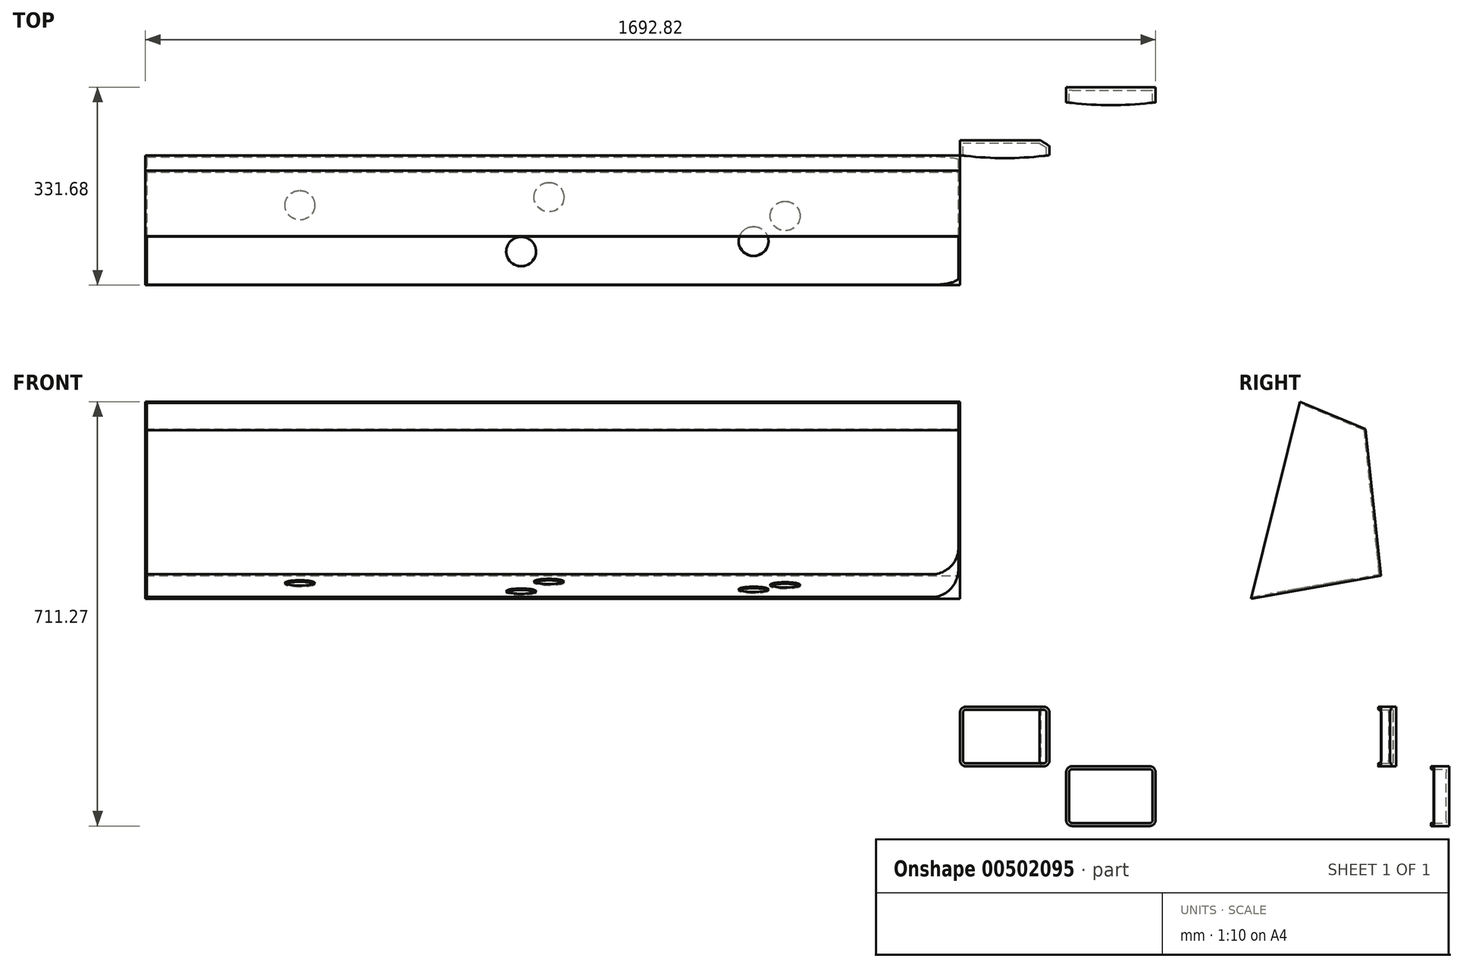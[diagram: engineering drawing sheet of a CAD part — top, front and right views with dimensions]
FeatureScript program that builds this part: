
annotation { "Feature Type Name" : "Feature", "Feature Type Description" : "" }
export const myFeature = defineFeature(function(context is Context, id is Id, definition is map)
    precondition{}
    {
        {
            var Q0;
            Q0=qCreatedBy(makeId("Front.planeOp"),FACE);
            var sketch = newSketch(context, id + "F0", { "sketchPlane" : qUnion([Q0])});
            skLineSegment(sketch, "E0.bottom", {"start": v(0, 0) * mm, "end": v(150, 0) * mm});
            skLineSegment(sketch, "E0.top", {"start": v(0, 100) * mm, "end": v(150, 100) * mm});
            skLineSegment(sketch, "E0.left", {"start": v(0, 0) * mm, "end": v(0, 100) * mm});
            skLineSegment(sketch, "E0.right", {"start": v(150, 0) * mm, "end": v(150, 100) * mm});
            skSolve(sketch);
        }
        {
            var Q0;
            Q0=makeQuery(id+"F0.imprint","IMPRINT",FACE,{"disambiguationData":[TD([[makeQuery(id+"F0.imprint","IMPRINT",EDGE,{"derivedFrom":sQuery(id+"F0.wireOp",EDGE,"E0.bottom")}),1.0]])]});
            extrude(context, id + "F1", {"entities" : qUnion([Q0]), "depth" : 30 * mm});
        }
        {
            var Q0;
            Q0=makeQuery(id+"F1.opExtrude","SWEPT_EDGE",EDGE,{"disambiguationData":[OSD([sQuery(id+"F0.wireOp",EDGE,"E0.top"),sQuery(id+"F0.wireOp",EDGE,"E0.left")])]});
            var Q1;
            Q1=makeQuery(id+"F1.opExtrude","SWEPT_EDGE",EDGE,{"disambiguationData":[OSD([sQuery(id+"F0.wireOp",EDGE,"E0.bottom"),sQuery(id+"F0.wireOp",EDGE,"E0.left")])]});
            var Q2;
            Q2=makeQuery(id+"F1.opExtrude","SWEPT_EDGE",EDGE,{"disambiguationData":[OSD([sQuery(id+"F0.wireOp",EDGE,"E0.bottom"),sQuery(id+"F0.wireOp",EDGE,"E0.right")])]});
            var Q3;
            Q3=makeQuery(id+"F1.opExtrude","SWEPT_EDGE",EDGE,{"disambiguationData":[OSD([sQuery(id+"F0.wireOp",EDGE,"E0.top"),sQuery(id+"F0.wireOp",EDGE,"E0.right")])]});
            fillet(context, id + "F2", {"entities" : qUnion([Q0, Q1, Q2, Q3]), "radius" : 10 * mm, "tangentPropagation" : true, "allowEdgeOverflow" : false});
        }
        {
            var Q0;
            Q0=makeQuery(id+"F1.opExtrude","CAP_FACE",FACE,{"disambiguationData":[OSD([sQuery(id+"F0.wireOp",EDGE,"E0.bottom"),sQuery(id+"F0.wireOp",EDGE,"E0.top"),sQuery(id+"F0.wireOp",EDGE,"E0.left"),sQuery(id+"F0.wireOp",EDGE,"E0.right")])],"isStart":false});
            shell(context, id + "F3", {"entities" : qUnion([Q0]), "thickness" : 5 * mm});
        }
        {
            var Q0;
            Q0=makeQuery(id+"F1.opExtrude","SWEPT_FACE",FACE,{"disambiguationData":[OSD([sQuery(id+"F0.wireOp",EDGE,"E0.bottom")])]});
            var sketch = newSketch(context, id + "F4", { "sketchPlane" : qUnion([Q0])});
            skLineSegment(sketch, "E1.0", {"start": v(10, 30) * mm, "end": v(140, 30) * mm});
            skLineSegment(sketch, "E2.0", {"start": v(0, 0) * mm, "end": v(0, 30) * mm});
            skLineSegment(sketch, "E3", {"start": v(75, 30) * mm, "end": v(75, -535) * mm});
            skCircle(sketch, "E4", {"center": v(75, -535) * mm, "radius": 565 * mm});
            skPoint(sketch, "E5", {"position": v(0, 25) * mm});
            skSolve(sketch);
        }
        {
            var Q0;
            {var subQ0=sQuery(id+"F0.wireOp",EDGE,"E0.bottom");var subQ1=makeQuery(id+"F1.opExtrude","CAP_EDGE",EDGE,{"disambiguationData":[OSD([subQ0])],"isStart":true});var subQ10=makeQuery(id+"F4.imprint","INTERSECT",VERTEX,{"derivedFrom":[subQ1,sQuery(id+"F4.wireOp",EDGE,"E3")]});Q0=makeQuery(id+"F4.imprint","IMPRINT",FACE,{"disambiguationData":[TD([[makeQuery(id+"F4.imprint","IMPRINT",EDGE,{"disambiguationData":[TD([[subQ10,1.0]])],"derivedFrom":subQ1}),-1.0]])]});}
            var Q1;
            {var subQ1=sQuery(id+"F4.wireOp",EDGE,"E3");var subQ3=sQuery(id+"F0.wireOp",EDGE,"E0.bottom");var subQ4=makeQuery(id+"F1.opExtrude","CAP_EDGE",EDGE,{"disambiguationData":[OSD([subQ3])],"isStart":true});var subQ5=makeQuery(id+"F4.imprint","INTERSECT",VERTEX,{"derivedFrom":[subQ4,subQ1]});Q1=makeQuery(id+"F4.imprint","IMPRINT",FACE,{"disambiguationData":[TD([[makeQuery(id+"F4.imprint","IMPRINT",EDGE,{"disambiguationData":[TD([[subQ5,1.0]])],"derivedFrom":subQ1}),1.0]])]});}
            var Q2;
            {var subQ1=sQuery(id+"F4.wireOp",EDGE,"E3");var subQ3=sQuery(id+"F0.wireOp",EDGE,"E0.bottom");var subQ4=makeQuery(id+"F1.opExtrude","CAP_EDGE",EDGE,{"disambiguationData":[OSD([subQ3])],"isStart":true});var subQ5=makeQuery(id+"F4.imprint","INTERSECT",VERTEX,{"derivedFrom":[subQ4,subQ1]});Q2=makeQuery(id+"F4.imprint","IMPRINT",FACE,{"disambiguationData":[TD([[makeQuery(id+"F4.imprint","IMPRINT",EDGE,{"disambiguationData":[TD([[subQ5,1.0]])],"derivedFrom":subQ1}),-1.0]])]});}
            extrude(context, id + "F5", {"entities" : qUnion([Q0, Q1, Q2]), "operationType" : NewBodyOperationType.INTERSECT, "oppositeDirection" : true, "depth" : 386 * mm});
        }
        {
            var Q0;
            Q0=makeQuery(id+"F1.opExtrude","SWEPT_FACE",FACE,{"disambiguationData":[OSD([sQuery(id+"F0.wireOp",EDGE,"E0.top")])]});
            var sketch = newSketch(context, id + "F6", { "sketchPlane" : qUnion([Q0])});
            skLineSegment(sketch, "E6.bottom", {"start": v(-27.82, -118.66) * mm, "end": v(-177.82, -118.66) * mm});
            skLineSegment(sketch, "E6.top", {"start": v(-27.82, -88.66) * mm, "end": v(-177.82, -88.66) * mm});
            skLineSegment(sketch, "E6.left", {"start": v(-27.82, -118.66) * mm, "end": v(-27.82, -88.66) * mm});
            skLineSegment(sketch, "E6.right", {"start": v(-177.82, -118.66) * mm, "end": v(-177.82, -88.66) * mm});
            skArc(sketch, "E7", {"start": v(-177.82, -113.66) * mm, "mid": v(-102.82, -118.66) * mm, "end": v(-27.82, -113.66) * mm});
            skPoint(sketch, "E8", {"position": v(-27.82, -113.66) * mm});
            skLineSegment(sketch, "E9", {"start": v(-102.82, -118.66) * mm, "end": v(-102.82, -64.18) * mm});
            skSolve(sketch);
        }
        {
            var Q0;
            {var subQ0=sQuery(id+"F6.wireOp",EDGE,"E6.left");var subQ1=sQuery(id+"F6.wireOp",EDGE,"E6.top");var subQ2=makeQuery(id+"F6.imprint","INTERSECT",VERTEX,{"derivedFrom":[subQ1,subQ0]});Q0=makeQuery(id+"F6.imprint","IMPRINT",FACE,{"disambiguationData":[TD([[makeQuery(id+"F6.imprint","IMPRINT",EDGE,{"disambiguationData":[TD([[subQ2,-1.0]])],"derivedFrom":subQ1}),1.0]])]});}
            var Q1;
            {var subQ0=sQuery(id+"F6.wireOp",EDGE,"E6.right");var subQ1=sQuery(id+"F6.wireOp",EDGE,"E6.top");var subQ2=makeQuery(id+"F6.imprint","INTERSECT",VERTEX,{"derivedFrom":[subQ1,subQ0]});Q1=makeQuery(id+"F6.imprint","IMPRINT",FACE,{"disambiguationData":[TD([[makeQuery(id+"F6.imprint","IMPRINT",EDGE,{"disambiguationData":[TD([[subQ2,1.0]])],"derivedFrom":subQ1}),1.0]])]});}
            extrude(context, id + "F7", {"entities" : qUnion([Q0, Q1]), "depth" : 100 * mm});
        }
        {
            var Q0;
            Q0=makeQuery(id+"F7.opExtrude","SWEPT_EDGE",EDGE,{"disambiguationData":[OSD([sQuery(id+"F6.wireOp",EDGE,"E6.top"),sQuery(id+"F6.wireOp",EDGE,"E6.left")])]});
            chamfer(context, id + "F8", {"entities" : qUnion([Q0]), "chamferType" : ChamferType.TWO_OFFSETS, "width1" : 15 * mm, "oppositeDirection" : false, "width2" : 10 * mm, "tangentPropagation" : true});
        }
        {
            var Q0;
            Q0=makeQuery(id+"F7.opExtrude","CAP_EDGE",EDGE,{"disambiguationData":[OSD([sQuery(id+"F6.wireOp",EDGE,"E6.left")])],"isStart":true});
            var Q1;
            Q1=makeQuery(id+"F7.opExtrude","CAP_EDGE",EDGE,{"disambiguationData":[OSD([sQuery(id+"F6.wireOp",EDGE,"E6.left")])],"isStart":false});
            var Q2;
            Q2=makeQuery(id+"F7.opExtrude","CAP_EDGE",EDGE,{"disambiguationData":[OSD([sQuery(id+"F6.wireOp",EDGE,"E6.right")])],"isStart":false});
            var Q3;
            Q3=makeQuery(id+"F7.opExtrude","CAP_EDGE",EDGE,{"disambiguationData":[OSD([sQuery(id+"F6.wireOp",EDGE,"E6.right")])],"isStart":true});
            fillet(context, id + "F9", {"entities" : qUnion([Q0, Q1, Q2, Q3]), "radius" : 10 * mm, "tangentPropagation" : true, "allowEdgeOverflow" : false});
        }
        {
            var Q0;
            Q0=makeQuery(id+"F7.opExtrude","SWEPT_FACE",FACE,{"disambiguationData":[OSD([sQuery(id+"F6.wireOp",EDGE,"E7")])]});
            shell(context, id + "F10", {"entities" : qUnion([Q0]), "thickness" : 5 * mm});
        }
        {
            var Q0;
            Q0=makeQuery(id+"F7.opExtrude","SWEPT_FACE",FACE,{"disambiguationData":[OSD([sQuery(id+"F6.wireOp",EDGE,"E6.right")])]});
            var sketch = newSketch(context, id + "F11", { "sketchPlane" : qUnion([Q0])});
            skLineSegment(sketch, "E10", {"start": v(249.63, 711.27) * mm, "end": v(331.68, 381) * mm});
            skLineSegment(sketch, "E11", {"start": v(331.68, 381) * mm, "end": v(114.2, 419.71) * mm});
            skLineSegment(sketch, "E12", {"start": v(114.2, 419.71) * mm, "end": v(139.8, 665.08) * mm});
            skLineSegment(sketch, "E13", {"start": v(139.8, 665.08) * mm, "end": v(249.63, 711.27) * mm});
            skSolve(sketch);
        }
        {
            var Q0;
            Q0=makeQuery(id+"F11.imprint","IMPRINT",FACE,{"disambiguationData":[TD([[makeQuery(id+"F11.imprint","IMPRINT",EDGE,{"derivedFrom":sQuery(id+"F11.wireOp",EDGE,"E10")}),-1.0]])]});
            extrude(context, id + "F12", {"entities" : qUnion([Q0]), "depth" : 1365 * mm});
        }
        {
            var Q0;
            Q0=makeQuery(id+"F12.opExtrude","SWEPT_FACE",FACE,{"disambiguationData":[OSD([sQuery(id+"F11.wireOp",EDGE,"E10")])]});
            shell(context, id + "F13", {"entities" : qUnion([Q0]), "thickness" : 2.5 * mm});
        }
        {
            var Q0;
            Q0=makeQuery(id+"F12.opExtrude","SWEPT_FACE",FACE,{"disambiguationData":[OSD([sQuery(id+"F11.wireOp",EDGE,"E11")])]});
            var sketch = newSketch(context, id + "F14", { "sketchPlane" : qUnion([Q0])});
            skPoint(sketch, "E14", {"position": v(-913.2, 202.16) * mm});
            skPoint(sketch, "E15", {"position": v(-866.53, 109.67) * mm});
            skPoint(sketch, "E16", {"position": v(-1284.06, 123.42) * mm});
            skPoint(sketch, "E17", {"position": v(-470.88, 141.68) * mm});
            skPoint(sketch, "E18", {"position": v(-523.75, 184.67) * mm});
            skSolve(sketch);
        }
        {
            var Q0;
            Q0=sQuery(id+"F14.wireOp",VERTEX,"E16");
            var Q1;
            Q1=sQuery(id+"F14.wireOp",VERTEX,"E15");
            var Q2;
            Q2=sQuery(id+"F14.wireOp",VERTEX,"E14");
            var Q3;
            Q3=sQuery(id+"F14.wireOp",VERTEX,"E18");
            var Q4;
            Q4=sQuery(id+"F14.wireOp",VERTEX,"E17");
            var Q5;
            Q5=makeQuery(id+"F12.opExtrude","SWEPT_BODY",BODY,{"disambiguationData":[OSD([sQuery(id+"F11.wireOp",EDGE,"E10"),sQuery(id+"F11.wireOp",EDGE,"E11"),sQuery(id+"F11.wireOp",EDGE,"E12"),sQuery(id+"F11.wireOp",EDGE,"E13")])]});
            hole(context, id + "F15", {"style" : HoleStyle.SIMPLE, "endStyle" : HoleEndStyle.BLIND, "holeDiameter" : 50 * mm, "holeDepth" : 12 * mm, "isTappedThrough" : true, "tappedDepth" : 12 * mm, "tapClearance" : 3, "locations" : qUnion([Q0, Q1, Q2, Q3, Q4]), "scope" : qUnion([Q5])});
        }
        {
            var Q0;
            {var subQ0=sQuery(id+"F11.wireOp",EDGE,"E11");Q0=makeQuery(id+"F13.opShell","OFFSET_EDGE",EDGE,{"disambiguationData":[OSD([subQ0]),TDD([makeQuery(id+"F12.opExtrude","CAP_EDGE",EDGE,{"disambiguationData":[OSD([subQ0])],"isStart":true})])]});}
            fillet(context, id + "F16", {"entities" : qUnion([Q0]), "radius" : 44.65 * mm, "tangentPropagation" : true, "allowEdgeOverflow" : false});
        }
    });
